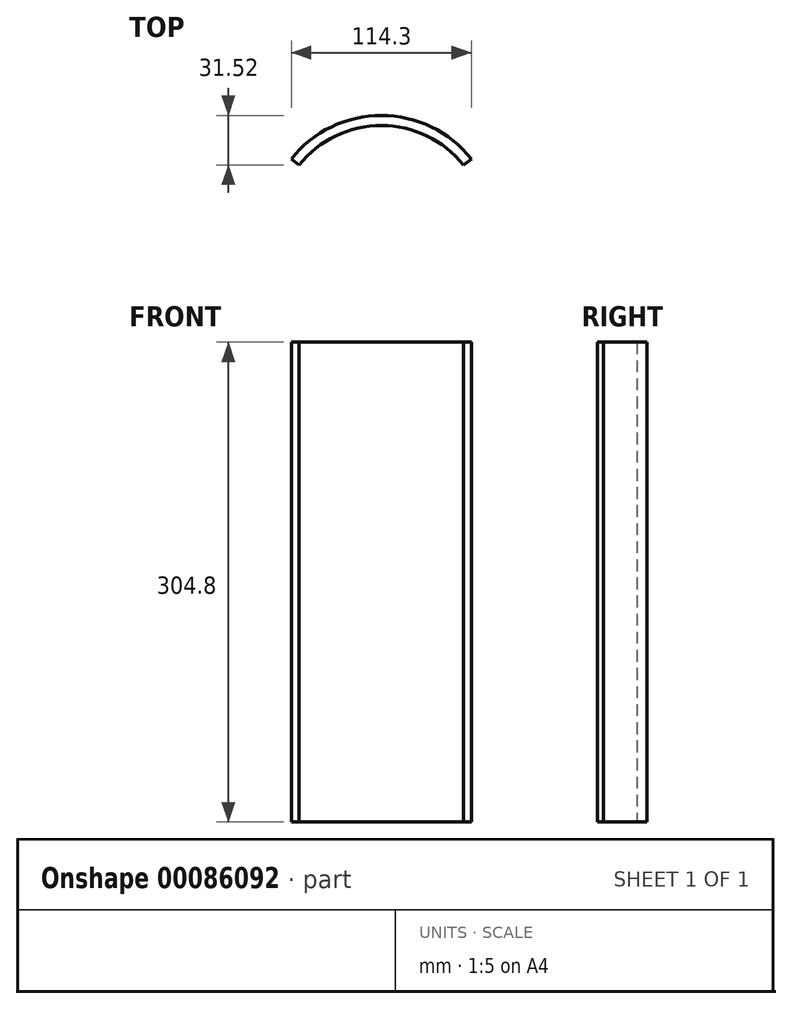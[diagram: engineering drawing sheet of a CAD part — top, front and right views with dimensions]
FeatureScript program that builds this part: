
annotation { "Feature Type Name" : "Feature", "Feature Type Description" : "" }
export const myFeature = defineFeature(function(context is Context, id is Id, definition is map)
    precondition{}
    {
        {
            var Q0;
            Q0=qCreatedBy(makeId("Top.planeOp"),FACE);
            var sketch = newSketch(context, id + "F0", { "sketchPlane" : qUnion([Q0])});
            skCircle(sketch, "E0", {"center": v(0, 0) * mm, "radius": 66.68 * mm});
            skCircle(sketch, "E1", {"center": v(0, 0) * mm, "radius": 73.03 * mm});
            skLineSegment(sketch, "E2", {"start": v(0, 0) * mm, "end": v(-51.64, 51.64) * mm, "construction": true});
            skLineSegment(sketch, "E3", {"start": v(-51.64, 51.64) * mm, "end": v(51.64, 51.64) * mm, "construction": true});
            skLineSegment(sketch, "E4", {"start": v(51.64, 51.64) * mm, "end": v(0, 0) * mm, "construction": true});
            skLineSegment(sketch, "E5", {"start": v(0, 0) * mm, "end": v(-57.15, 45.46) * mm});
            skLineSegment(sketch, "E6", {"start": v(0, 0) * mm, "end": v(57.15, 45.46) * mm});
            skLineSegment(sketch, "E7", {"start": v(0, 0) * mm, "end": v(0, 73.03) * mm, "construction": true});
            skPoint(sketch, "E7.endSnap0", {"position": v(0, 51.64) * mm});
            skSolve(sketch);
        }
        {
            var Q0;
            {var subQ0=sQuery(id+"F0.wireOp",EDGE,"E5");var subQ1=sQuery(id+"F0.wireOp",EDGE,"E0");var subQ2=makeQuery(id+"F0.imprint","INTERSECT",VERTEX,{"derivedFrom":[subQ1,subQ0]});Q0=makeQuery(id+"F0.imprint","IMPRINT",FACE,{"disambiguationData":[TD([[makeQuery(id+"F0.imprint","IMPRINT",EDGE,{"disambiguationData":[TD([[subQ2,1.0]])],"derivedFrom":subQ1}),-1.0]])]});}
            extrude(context, id + "F1", {"entities" : qUnion([Q0]), "endBound" : BoundingType.SYMMETRIC, "depth" : 304.8 * mm});
        }
    });
